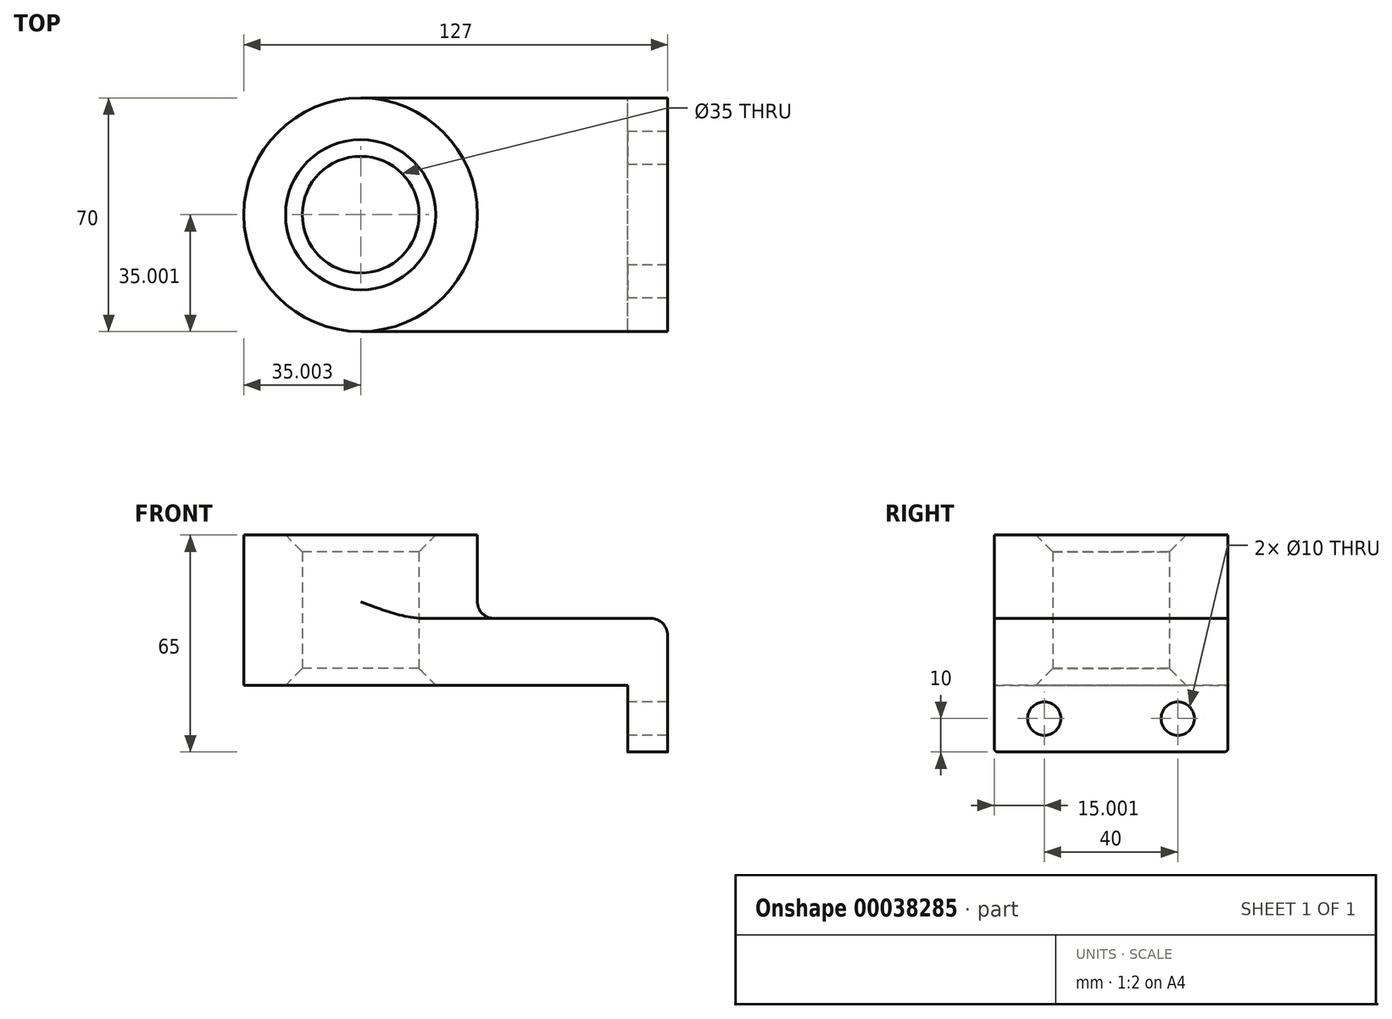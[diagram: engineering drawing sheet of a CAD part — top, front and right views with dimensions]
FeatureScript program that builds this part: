
annotation { "Feature Type Name" : "Feature", "Feature Type Description" : "" }
export const myFeature = defineFeature(function(context is Context, id is Id, definition is map)
    precondition{}
    {
        {
            var Q0;
            Q0=qCreatedBy(makeId("Top.planeOp"),FACE);
            var sketch = newSketch(context, id + "F0", { "sketchPlane" : qUnion([Q0])});
            skLineSegment(sketch, "E0.bottom", {"start": v(-98.8, 14.28) * mm, "end": v(-178.8, 14.28) * mm});
            skLineSegment(sketch, "E0.top", {"start": v(-98.8, 84.28) * mm, "end": v(-178.8, 84.28) * mm});
            skLineSegment(sketch, "E0.left", {"start": v(-98.8, 14.28) * mm, "end": v(-98.8, 84.28) * mm});
            skLineSegment(sketch, "E0.right", {"start": v(-178.8, 14.28) * mm, "end": v(-178.8, 84.28) * mm});
            skCircle(sketch, "E1", {"center": v(-178.8, 49.28) * mm, "radius": 35 * mm});
            skCircle(sketch, "E2", {"center": v(-178.8, 49.28) * mm, "radius": 22.5 * mm});
            skCircle(sketch, "E3", {"center": v(-178.8, 49.28) * mm, "radius": 17.5 * mm});
            skSolve(sketch);
        }
        {
            var Q0;
            {var subQ3=sQuery(id+"F0.wireOp",EDGE,"E0.bottom");Q0=makeQuery(id+"F0.imprint","IMPRINT",FACE,{"disambiguationData":[TD([[makeQuery(id+"F0.imprint","IMPRINT",EDGE,{"derivedFrom":subQ3}),-1.0]])]});}
            var Q1;
            {var subQ1=sQuery(id+"F0.wireOp",EDGE,"E0.right");var subQ4=sQuery(id+"F0.wireOp",EDGE,"E2");var subQ6=makeQuery(id+"F0.imprint","INTERSECT",VERTEX,{"disambiguationData":[OD(0.0)],"derivedFrom":[subQ1,subQ4]});Q1=makeQuery(id+"F0.imprint","IMPRINT",FACE,{"disambiguationData":[TD([[makeQuery(id+"F0.imprint","IMPRINT",EDGE,{"disambiguationData":[TD([[subQ6,-1.0]])],"derivedFrom":subQ1}),-1.0]])]});}
            var Q2;
            {var subQ0=sQuery(id+"F0.wireOp",EDGE,"E2");var subQ1=sQuery(id+"F0.wireOp",EDGE,"E0.right");var subQ3=makeQuery(id+"F0.imprint","INTERSECT",VERTEX,{"disambiguationData":[OD(0.0)],"derivedFrom":[subQ1,subQ0]});Q2=makeQuery(id+"F0.imprint","IMPRINT",FACE,{"disambiguationData":[TD([[makeQuery(id+"F0.imprint","IMPRINT",EDGE,{"disambiguationData":[TD([[subQ3,-1.0]])],"derivedFrom":subQ0}),-1.0]])]});}
            var Q3;
            {var subQ1=sQuery(id+"F0.wireOp",EDGE,"E0.right");var subQ4=sQuery(id+"F0.wireOp",EDGE,"E2");var subQ6=makeQuery(id+"F0.imprint","INTERSECT",VERTEX,{"disambiguationData":[OD(0.0)],"derivedFrom":[subQ1,subQ4]});Q3=makeQuery(id+"F0.imprint","IMPRINT",FACE,{"disambiguationData":[TD([[makeQuery(id+"F0.imprint","IMPRINT",EDGE,{"disambiguationData":[TD([[subQ6,-1.0]])],"derivedFrom":subQ1}),1.0]])]});}
            var Q4;
            {var subQ0=sQuery(id+"F0.wireOp",EDGE,"E2");var subQ1=sQuery(id+"F0.wireOp",EDGE,"E0.right");var subQ3=makeQuery(id+"F0.imprint","INTERSECT",VERTEX,{"disambiguationData":[OD(0.0)],"derivedFrom":[subQ1,subQ0]});Q4=makeQuery(id+"F0.imprint","IMPRINT",FACE,{"disambiguationData":[TD([[makeQuery(id+"F0.imprint","IMPRINT",EDGE,{"disambiguationData":[TD([[subQ3,1.0]])],"derivedFrom":subQ0}),-1.0]])]});}
            extrude(context, id + "F1", {"entities" : qUnion([Q0, Q1, Q2, Q3, Q4]), "depth" : 20 * mm});
        }
        {
            var Q0;
            {var subQ0=sQuery(id+"F0.wireOp",EDGE,"E2");var subQ1=sQuery(id+"F0.wireOp",EDGE,"E0.right");var subQ3=makeQuery(id+"F0.imprint","INTERSECT",VERTEX,{"disambiguationData":[OD(0.0)],"derivedFrom":[subQ1,subQ0]});Q0=makeQuery(id+"F0.imprint","IMPRINT",FACE,{"disambiguationData":[TD([[makeQuery(id+"F0.imprint","IMPRINT",EDGE,{"disambiguationData":[TD([[subQ3,1.0]])],"derivedFrom":subQ0}),-1.0]])]});}
            var Q1;
            {var subQ1=sQuery(id+"F0.wireOp",EDGE,"E0.right");var subQ4=sQuery(id+"F0.wireOp",EDGE,"E2");var subQ6=makeQuery(id+"F0.imprint","INTERSECT",VERTEX,{"disambiguationData":[OD(0.0)],"derivedFrom":[subQ1,subQ4]});Q1=makeQuery(id+"F0.imprint","IMPRINT",FACE,{"disambiguationData":[TD([[makeQuery(id+"F0.imprint","IMPRINT",EDGE,{"disambiguationData":[TD([[subQ6,-1.0]])],"derivedFrom":subQ1}),1.0]])]});}
            var Q2;
            {var subQ1=sQuery(id+"F0.wireOp",EDGE,"E0.right");var subQ4=sQuery(id+"F0.wireOp",EDGE,"E2");var subQ6=makeQuery(id+"F0.imprint","INTERSECT",VERTEX,{"disambiguationData":[OD(0.0)],"derivedFrom":[subQ1,subQ4]});Q2=makeQuery(id+"F0.imprint","IMPRINT",FACE,{"disambiguationData":[TD([[makeQuery(id+"F0.imprint","IMPRINT",EDGE,{"disambiguationData":[TD([[subQ6,-1.0]])],"derivedFrom":subQ1}),-1.0]])]});}
            var Q3;
            {var subQ0=sQuery(id+"F0.wireOp",EDGE,"E2");var subQ1=sQuery(id+"F0.wireOp",EDGE,"E0.right");var subQ3=makeQuery(id+"F0.imprint","INTERSECT",VERTEX,{"disambiguationData":[OD(0.0)],"derivedFrom":[subQ1,subQ0]});Q3=makeQuery(id+"F0.imprint","IMPRINT",FACE,{"disambiguationData":[TD([[makeQuery(id+"F0.imprint","IMPRINT",EDGE,{"disambiguationData":[TD([[subQ3,-1.0]])],"derivedFrom":subQ0}),-1.0]])]});}
            extrude(context, id + "F2", {"entities" : qUnion([Q0, Q1, Q2, Q3]), "operationType" : NewBodyOperationType.ADD, "depth" : 45 * mm});
        }
        {
            var Q0;
            Q0=makeQuery(id+"F1.opExtrude","SWEPT_FACE",FACE,{"disambiguationData":[OSD([sQuery(id+"F0.wireOp",EDGE,"E0.left")])]});
            var sketch = newSketch(context, id + "F3", { "sketchPlane" : qUnion([Q0])});
            skLineSegment(sketch, "E4.bottom", {"start": v(14.28, 20) * mm, "end": v(84.28, 20) * mm});
            skLineSegment(sketch, "E4.top", {"start": v(14.28, -20) * mm, "end": v(84.28, -20) * mm});
            skLineSegment(sketch, "E4.left", {"start": v(14.28, 20) * mm, "end": v(14.28, -20) * mm});
            skLineSegment(sketch, "E4.right", {"start": v(84.28, 20) * mm, "end": v(84.28, -20) * mm});
            skCircle(sketch, "E5", {"center": v(29.28, -10) * mm, "radius": 5 * mm});
            skLineSegment(sketch, "E6", {"start": v(49.28, -20) * mm, "end": v(49.28, 51.61) * mm});
            skCircle(sketch, "E7.MirrorC", {"center": v(69.28, -10) * mm, "radius": 5 * mm});
            skSolve(sketch);
        }
        {
            var Q0;
            Q0 = qSketchRegion(id + "F3", true);
            extrude(context, id + "F4", {"entities" : qUnion([Q0]), "operationType" : NewBodyOperationType.ADD, "depth" : 12 * mm});
        }
        {
            var Q0;
            Q0=makeQuery(id+"F4.opExtrude","SWEPT_EDGE",EDGE,{"disambiguationData":[OSD([sQuery(id+"F3.wireOp",EDGE,"E4.top"),sQuery(id+"F3.wireOp",EDGE,"E4.right")])]});
            var Q1;
            Q1=makeQuery(id+"F4.opExtrude","SWEPT_EDGE",EDGE,{"disambiguationData":[OSD([sQuery(id+"F3.wireOp",EDGE,"E4.top"),sQuery(id+"F3.wireOp",EDGE,"E4.left")])]});
            var Q2;
            Q2=makeQuery(id+"F1.opExtrude","CAP_EDGE",EDGE,{"disambiguationData":[OSD([sQuery(id+"F0.wireOp",EDGE,"E0.left")])],"isStart":true});
            fillet(context, id + "F5", {"entities" : qUnion([Q0, Q1, Q2]), "radius" : 1 * mm, "tangentPropagation" : true, "allowEdgeOverflow" : false});
        }
        {
            var Q0;
            Q0=makeQuery(id+"F4.opExtrude","CAP_EDGE",EDGE,{"disambiguationData":[OSD([sQuery(id+"F3.wireOp",EDGE,"E4.bottom")])],"isStart":false});
            var Q1;
            {var subQ0=sQuery(id+"F0.wireOp",EDGE,"E1");Q1=makeQuery(id+"F2.boolean.opBoolean","INTERSECT",EDGE,{"derivedFrom":[makeQuery(id+"F1.opExtrude","CAP_FACE",FACE,{"disambiguationData":[OSD([sQuery(id+"F0.wireOp",EDGE,"E0.bottom"),sQuery(id+"F0.wireOp",EDGE,"E0.top"),sQuery(id+"F0.wireOp",EDGE,"E0.left"),subQ0,sQuery(id+"F0.wireOp",EDGE,"E3")])],"isStart":false}),makeQuery(id+"F2.opExtrude","SWEPT_FACE",FACE,{"disambiguationData":[OSD([subQ0])]})]});}
            fillet(context, id + "F6", {"entities" : qUnion([Q0, Q1]), "radius" : 5 * mm, "tangentPropagation" : true, "allowEdgeOverflow" : false});
        }
        {
            var Q0;
            {var subQ0=sQuery(id+"F0.wireOp",EDGE,"E3");Q0=makeQuery(id+"F2.boolean.opBoolean","MERGE",FACE,{"derivedFrom":[makeQuery(id+"F1.opExtrude","SWEPT_FACE",FACE,{"disambiguationData":[OSD([subQ0])]}),makeQuery(id+"F2.opExtrude","SWEPT_FACE",FACE,{"disambiguationData":[OSD([subQ0])]})]});}
            chamfer(context, id + "F7", {"entities" : qUnion([Q0]), "width" : 5 * mm, "tangentPropagation" : true});
        }
    });
